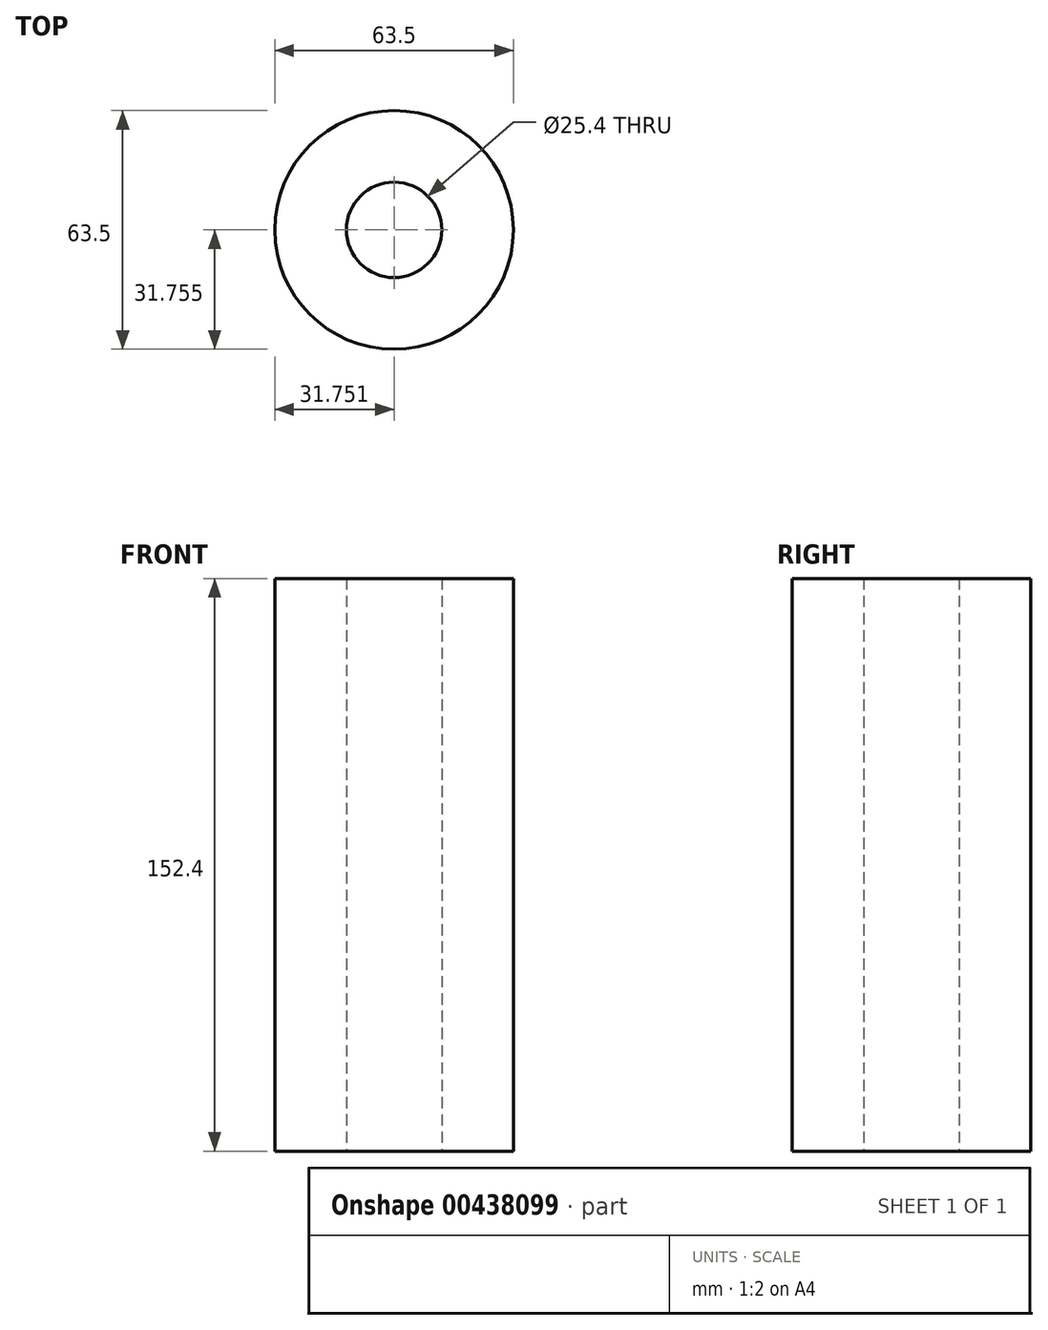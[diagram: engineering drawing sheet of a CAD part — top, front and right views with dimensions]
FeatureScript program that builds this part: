
annotation { "Feature Type Name" : "Feature", "Feature Type Description" : "" }
export const myFeature = defineFeature(function(context is Context, id is Id, definition is map)
    precondition{}
    {
        {
            var Q0;
            Q0=qCreatedBy(makeId("Top.planeOp"),FACE);
            var sketch = newSketch(context, id + "F0", { "sketchPlane" : qUnion([Q0])});
            skCircle(sketch, "E0", {"center": v(-0.3, 0.15) * mm, "radius": 31.75 * mm});
            skCircle(sketch, "E1", {"center": v(-0.3, 0.15) * mm, "radius": 12.7 * mm});
            skSolve(sketch);
        }
        {
            var Q0;
            Q0 = qSketchRegion(id + "F0", true);
            extrude(context, id + "F1", {"entities" : qUnion([Q0]), "depth" : 152.4 * mm});
        }
    });
